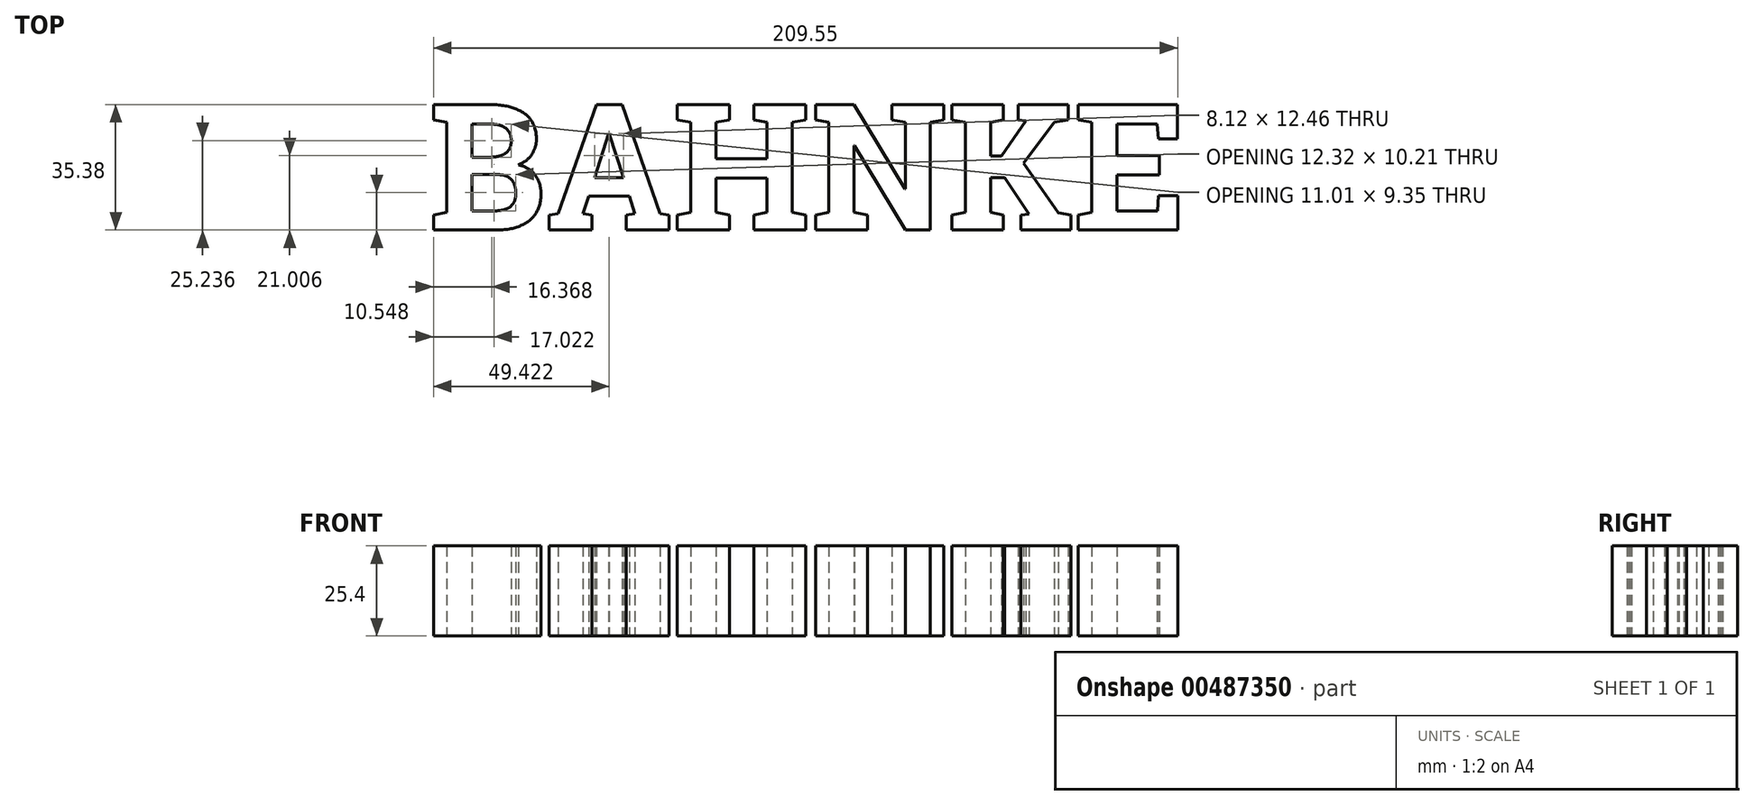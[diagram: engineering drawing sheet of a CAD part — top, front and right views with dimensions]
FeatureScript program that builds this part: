
annotation { "Feature Type Name" : "Feature", "Feature Type Description" : "" }
export const myFeature = defineFeature(function(context is Context, id is Id, definition is map)
    precondition{}
    {
        {
            var Q0;
            Q0=qCreatedBy(makeId("Top.planeOp"),FACE);
            var sketch = newSketch(context, id + "F0", { "sketchPlane" : qUnion([Q0])});
            skText(sketch, "E0", { "text": "BAHNKE", "fontName": "RobotoSlab-Bold.ttf"});
            const initialGuessF0  = {"E0": [-0.107, 0, 1, 0, 0.03583]};
            skSetInitialGuess(sketch, initialGuessF0);
            skSolve(sketch);
        }
        {
            var Q0;
            Q0 = qSketchRegion(id + "F0", true);
            extrude(context, id + "F1", {"entities" : qUnion([Q0]), "depth" : 25.4 * mm});
        }
    });
